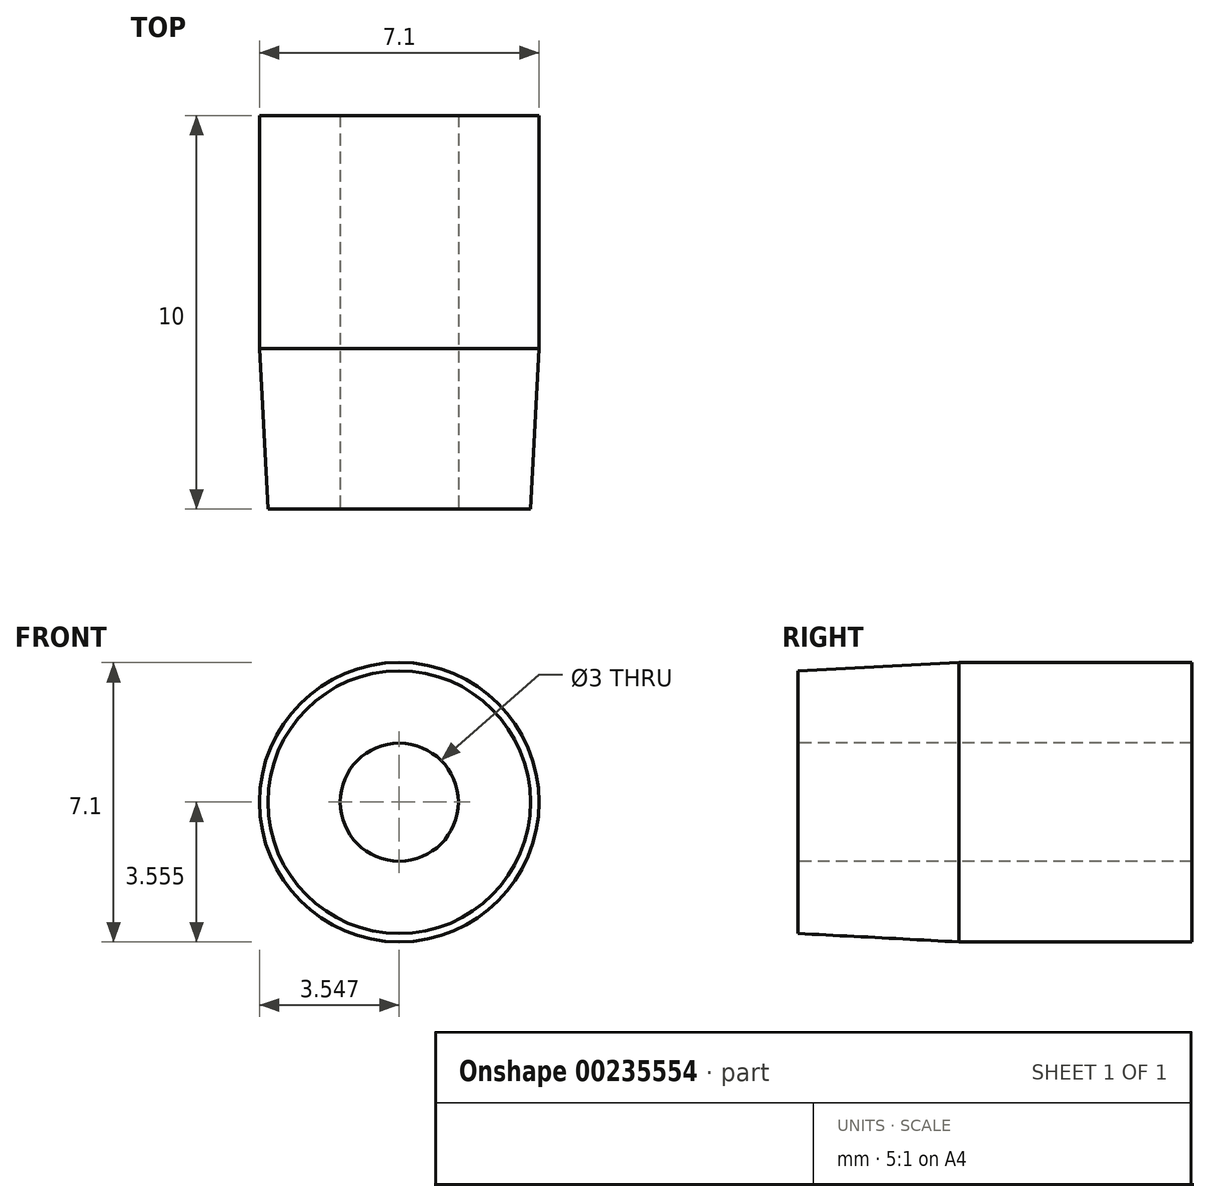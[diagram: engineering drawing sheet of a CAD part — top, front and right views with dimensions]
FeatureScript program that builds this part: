
annotation { "Feature Type Name" : "Feature", "Feature Type Description" : "" }
export const myFeature = defineFeature(function(context is Context, id is Id, definition is map)
    precondition{}
    {
        {
            var Q0;
            Q0=qCreatedBy(makeId("Front.planeOp"),FACE);
            var sketch = newSketch(context, id + "F0", { "sketchPlane" : qUnion([Q0])});
            skCircle(sketch, "E0", {"center": v(-36.08, 37.07) * mm, "radius": 3.55 * mm});
            skSolve(sketch);
        }
        {
            var Q0;
            Q0 = qSketchRegion(id + "F0", true);
            extrude(context, id + "F1", {"entities" : qUnion([Q0]), "depth" : 25 * mm});
        }
        {
            var Q0;
            Q0=makeQuery(id+"F1.opExtrude","CAP_EDGE",EDGE,{"disambiguationData":[OSD([sQuery(id+"F0.wireOp",EDGE,"E0")])],"isStart":false});
            chamfer(context, id + "F2", {"entities" : qUnion([Q0]), "chamferType" : ChamferType.OFFSET_ANGLE, "width" : 1 * mm, "oppositeDirection" : false, "angle" : 87 * degree, "tangentPropagation" : true});
        }
        {
            var Q0;
            Q0=makeQuery(id+"F1.opExtrude","CAP_FACE",FACE,{"disambiguationData":[OSD([sQuery(id+"F0.wireOp",EDGE,"E0")])],"isStart":false});
            var sketch = newSketch(context, id + "F3", { "sketchPlane" : qUnion([Q0])});
            skCircle(sketch, "E1", {"center": v(-36.08, 37.07) * mm, "radius": 4.5 * mm});
            skSolve(sketch);
        }
        {
            var Q0;
            Q0 = qSketchRegion(id + "F3", true);
            extrude(context, id + "F4", {"entities" : qUnion([Q0]), "operationType" : NewBodyOperationType.REMOVE, "oppositeDirection" : true, "depth" : 15 * mm});
        }
        {
            var Q0;
            Q0=makeQuery(id+"F4.boolean.opBoolean","COPY",FACE,{"derivedFrom":makeQuery(id+"F4.opExtrude","CAP_FACE",FACE,{"disambiguationData":[OSD([sQuery(id+"F3.wireOp",EDGE,"E1")])],"isStart":false})});
            var sketch = newSketch(context, id + "F5", { "sketchPlane" : qUnion([Q0])});
            skCircle(sketch, "E2", {"center": v(-36.08, 37.07) * mm, "radius": 1.5 * mm});
            skSolve(sketch);
        }
        {
            var Q0;
            Q0 = qSketchRegion(id + "F5", true);
            extrude(context, id + "F6", {"entities" : qUnion([Q0]), "operationType" : NewBodyOperationType.REMOVE, "oppositeDirection" : true, "depth" : 25 * mm});
        }
    });
